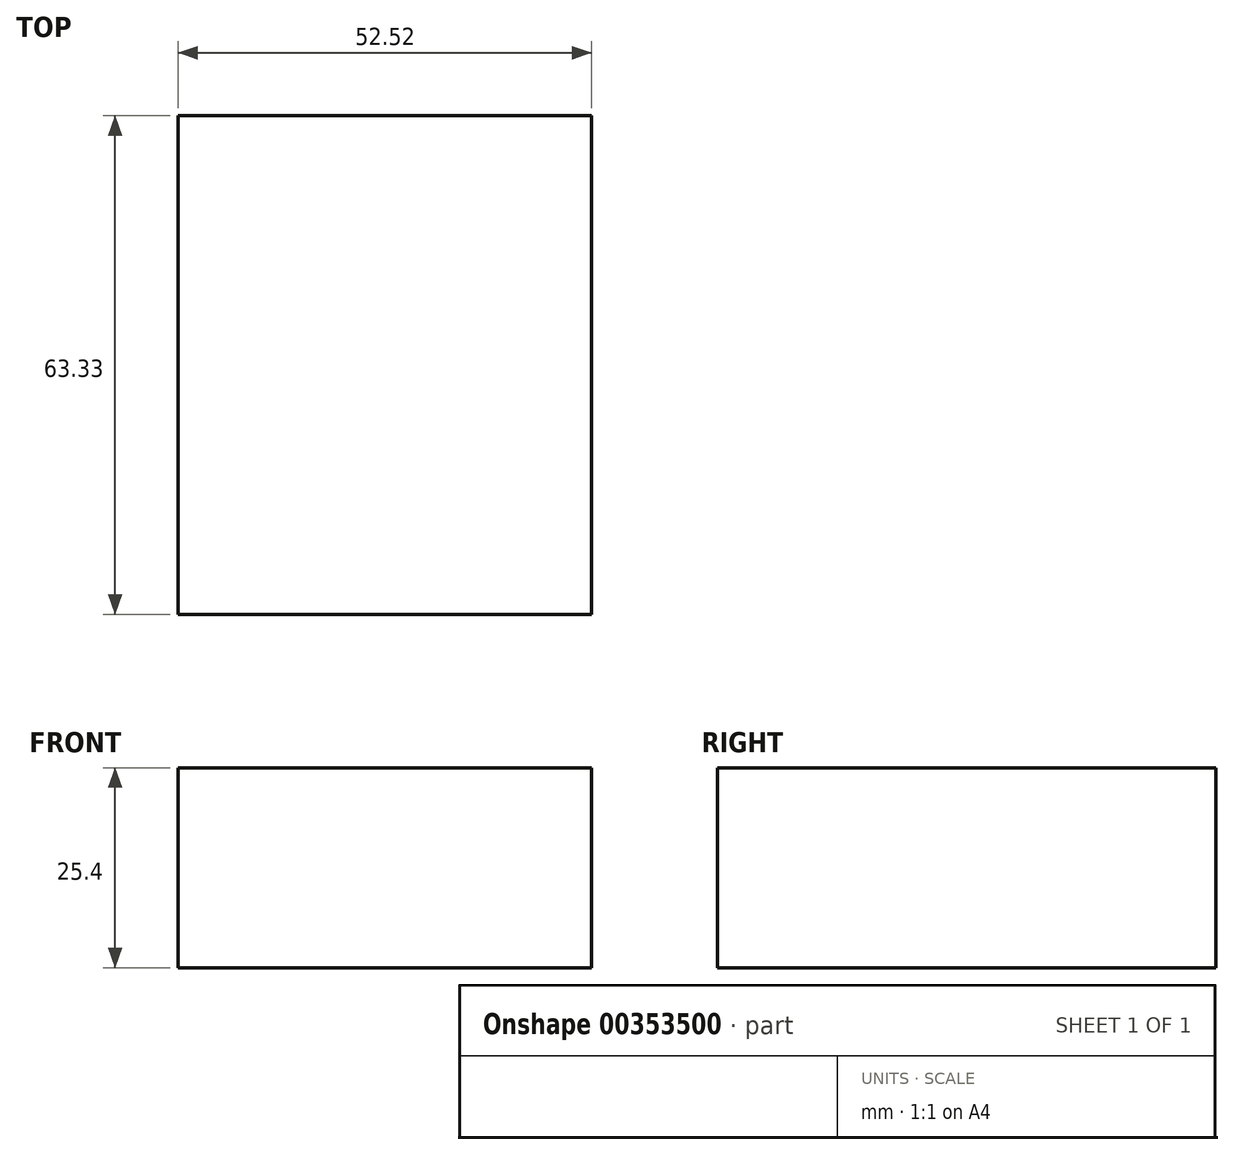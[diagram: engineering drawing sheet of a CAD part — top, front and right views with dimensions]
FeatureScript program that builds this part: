
annotation { "Feature Type Name" : "Feature", "Feature Type Description" : "" }
export const myFeature = defineFeature(function(context is Context, id is Id, definition is map)
    precondition{}
    {
        {
            var Q0;
            Q0=qCreatedBy(makeId("Top.planeOp"),FACE);
            var sketch = newSketch(context, id + "F0", { "sketchPlane" : qUnion([Q0])});
            skLineSegment(sketch, "E0.bottom", {"start": v(0, 0) * mm, "end": v(52.52, 0) * mm});
            skLineSegment(sketch, "E0.top", {"start": v(0, 63.33) * mm, "end": v(52.52, 63.33) * mm});
            skLineSegment(sketch, "E0.left", {"start": v(0, 0) * mm, "end": v(0, 63.33) * mm});
            skLineSegment(sketch, "E0.right", {"start": v(52.52, 0) * mm, "end": v(52.52, 63.33) * mm});
            skSolve(sketch);
        }
        {
            var Q0;
            Q0 = qSketchRegion(id + "F0", true);
            extrude(context, id + "F1", {"entities" : qUnion([Q0]), "depth" : 25.4 * mm});
        }
    });
